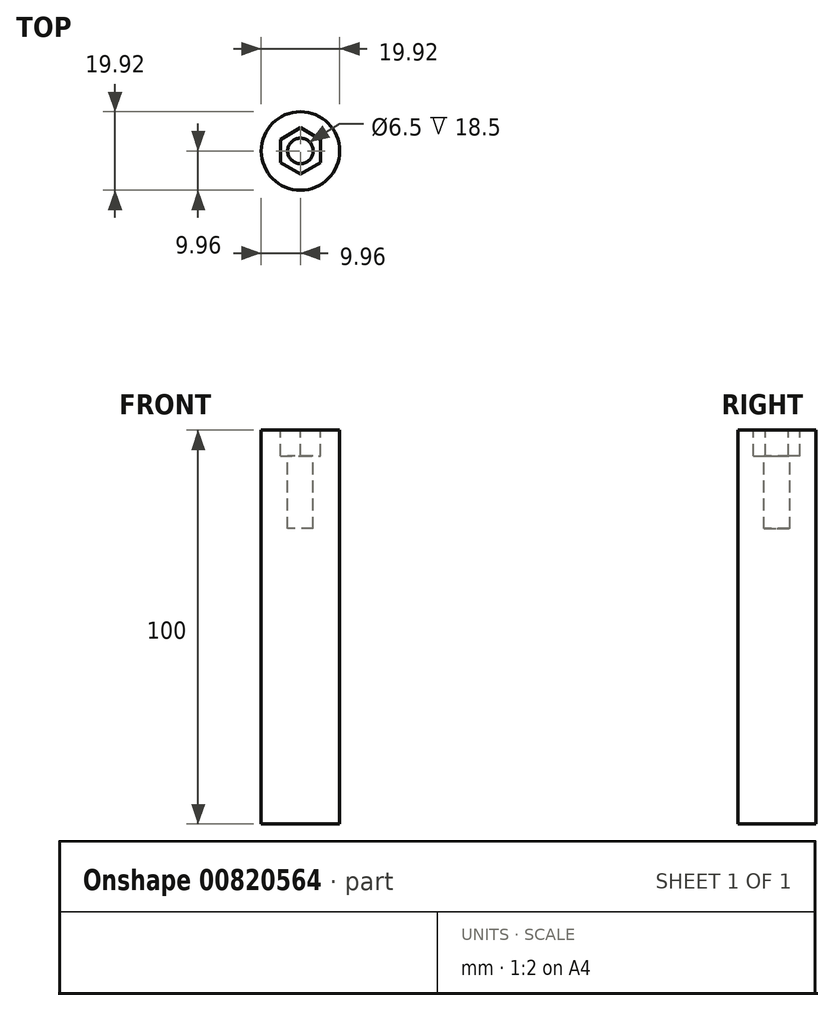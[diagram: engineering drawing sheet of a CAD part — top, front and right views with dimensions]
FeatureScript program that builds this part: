
annotation { "Feature Type Name" : "Feature", "Feature Type Description" : "" }
export const myFeature = defineFeature(function(context is Context, id is Id, definition is map)
    precondition{}
    {
        {
            var Q0;
            Q0=qCreatedBy(makeId("Top.planeOp"),FACE);
            var sketch = newSketch(context, id + "F0", { "sketchPlane" : qUnion([Q0])});
            skCircle(sketch, "E0", {"center": v(0, 0) * mm, "radius": 9.96 * mm});
            skSolve(sketch);
        }
        {
            var Q0;
            Q0=makeQuery(id+"F0.imprint","IMPRINT",FACE,{"disambiguationData":[TD([[makeQuery(id+"F0.imprint","IMPRINT",EDGE,{"derivedFrom":sQuery(id+"F0.wireOp",EDGE,"E0")}),1.0]])]});
            extrude(context, id + "F1", {"entities" : qUnion([Q0]), "depth" : 100 * mm, "offsetDistance" : 25 * mm});
        }
        {
            var Q0;
            Q0=makeQuery(id+"F1.opExtrude","CAP_FACE",FACE,{"disambiguationData":[OSD([sQuery(id+"F0.wireOp",EDGE,"E0")])],"isStart":false});
            var sketch = newSketch(context, id + "F2", { "sketchPlane" : qUnion([Q0])});
            skCircle(sketch, "E1", {"center": v(0, 0) * mm, "radius": 3.25 * mm});
            skSolve(sketch);
        }
        {
            var Q0;
            Q0=makeQuery(id+"F2.imprint","IMPRINT",FACE,{"disambiguationData":[TD([[makeQuery(id+"F2.imprint","IMPRINT",EDGE,{"derivedFrom":sQuery(id+"F2.wireOp",EDGE,"E1")}),1.0]])]});
            extrude(context, id + "F3", {"entities" : qUnion([Q0]), "operationType" : NewBodyOperationType.REMOVE, "oppositeDirection" : true, "depth" : 25 * mm, "offsetDistance" : 25 * mm});
        }
        {
            var Q0;
            Q0=makeQuery(id+"F1.opExtrude","CAP_FACE",FACE,{"disambiguationData":[OSD([sQuery(id+"F0.wireOp",EDGE,"E0")])],"isStart":false});
            var sketch = newSketch(context, id + "F4", { "sketchPlane" : qUnion([Q0])});
            skCircle(sketch, "E2.cCircle", {"center": v(0, 0) * mm, "radius": 5.9 * mm, "construction": true});
            skLineSegment(sketch, "E2.0", {"start": v(0, 5.9) * mm, "end": v(5.1, 2.95) * mm});
            skLineSegment(sketch, "E2.1", {"start": v(5.1, 2.95) * mm, "end": v(5.1, -2.95) * mm});
            skLineSegment(sketch, "E2.2", {"start": v(5.1, -2.95) * mm, "end": v(0, -5.9) * mm});
            skLineSegment(sketch, "E2.3", {"start": v(0, -5.9) * mm, "end": v(-5.1, -2.95) * mm});
            skLineSegment(sketch, "E2.4", {"start": v(-5.1, -2.95) * mm, "end": v(-5.1, 2.95) * mm});
            skLineSegment(sketch, "E2.5", {"start": v(-5.1, 2.95) * mm, "end": v(0, 5.9) * mm});
            skSolve(sketch);
        }
        {
            var Q0;
            Q0=makeQuery(id+"F4.imprint","IMPRINT",FACE,{"disambiguationData":[TD([[makeQuery(id+"F4.imprint","IMPRINT",EDGE,{"derivedFrom":sQuery(id+"F4.wireOp",EDGE,"E2.0")}),-1.0]])]});
            extrude(context, id + "F5", {"entities" : qUnion([Q0]), "operationType" : NewBodyOperationType.REMOVE, "oppositeDirection" : true, "depth" : 6.5 * mm, "offsetDistance" : 25 * mm});
        }
    });
